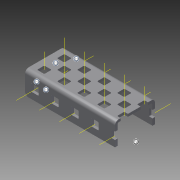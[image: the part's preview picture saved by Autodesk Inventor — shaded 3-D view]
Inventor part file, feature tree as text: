
AUTODESK INVENTOR PART (.ipt)
format: ipt  version: 2015 (Build 190159000, 159)  size: 1,938,944 bytes
history: native  units: in
note: dims shown in document units (in); Inventor stores cm internally (conversion verified against a paired STEP export)
features: other x31, pattern_linear x3, sheet_metal_op x1, extrude x1, imported_body x1, sketch x1
ambient origin geometry x8: Origin, YZ Plane, XZ Plane, XY Plane, X Axis, Y Axis, Z Axis, Center Point
bodies: Body1 (feature_tree)
feature tree (38):
  sheet_metal_op  "Fold1"
  other  "C-Channel"
  extrude  "length cut"  Depth=0.5in
  other  "top axis"
  other  "inner axis"
  other  "front axis"
  other  "back axis"
  pattern_linear  "top axes"  Spacing1=0.5in  [1 undecoded]
  pattern_linear  "inner axes"  Spacing1=0.5in  [1 undecoded]
  pattern_linear  "horiz axes"  Spacing1=-2.25in  [1 undecoded]
  other  "right plane"
  imported_body  "Base1"
  sketch  "Sketch1"  dims[d1=0.0in d4=0.5in d5=0.7874in d7=0.5in d10=0.5in d13=0.5in d14=-2.25in d15=0.0in d16=0.0in d17=0.0in d18=0.0in d19=0.0in]
  other  "Work Point1"
  other  "Work Point2"
  other  "Work Point3"
  other  "Work Point4"
  other  "Work Axis5"
  other  "Work Axis6"
  other  "Work Axis7"
  other  "Work Axis11"
  other  "Work Axis12"
  other  "Work Axis13"
  other  "Work Axis14"
  other  "Work Axis18"
  other  "Work Axis19"
  other  "Work Axis23"
  other  "Work Axis24"
  other  "Work Axis25"
  other  "Work Axis30"
  other  "Work Axis31"
  other  "Work Axis32"
  other  "left plane"
  other  "Work Axis137"
  other  "Work Axis138"
  other  "Work Axis139"
  other  "Work Axis140"
  other  "Work Axis141"
note: 3 required parameter values undecoded (feature->parameter linkage not recoverable at this tier; creation-order binding heuristic only, values carry confidence <= 0.55)
